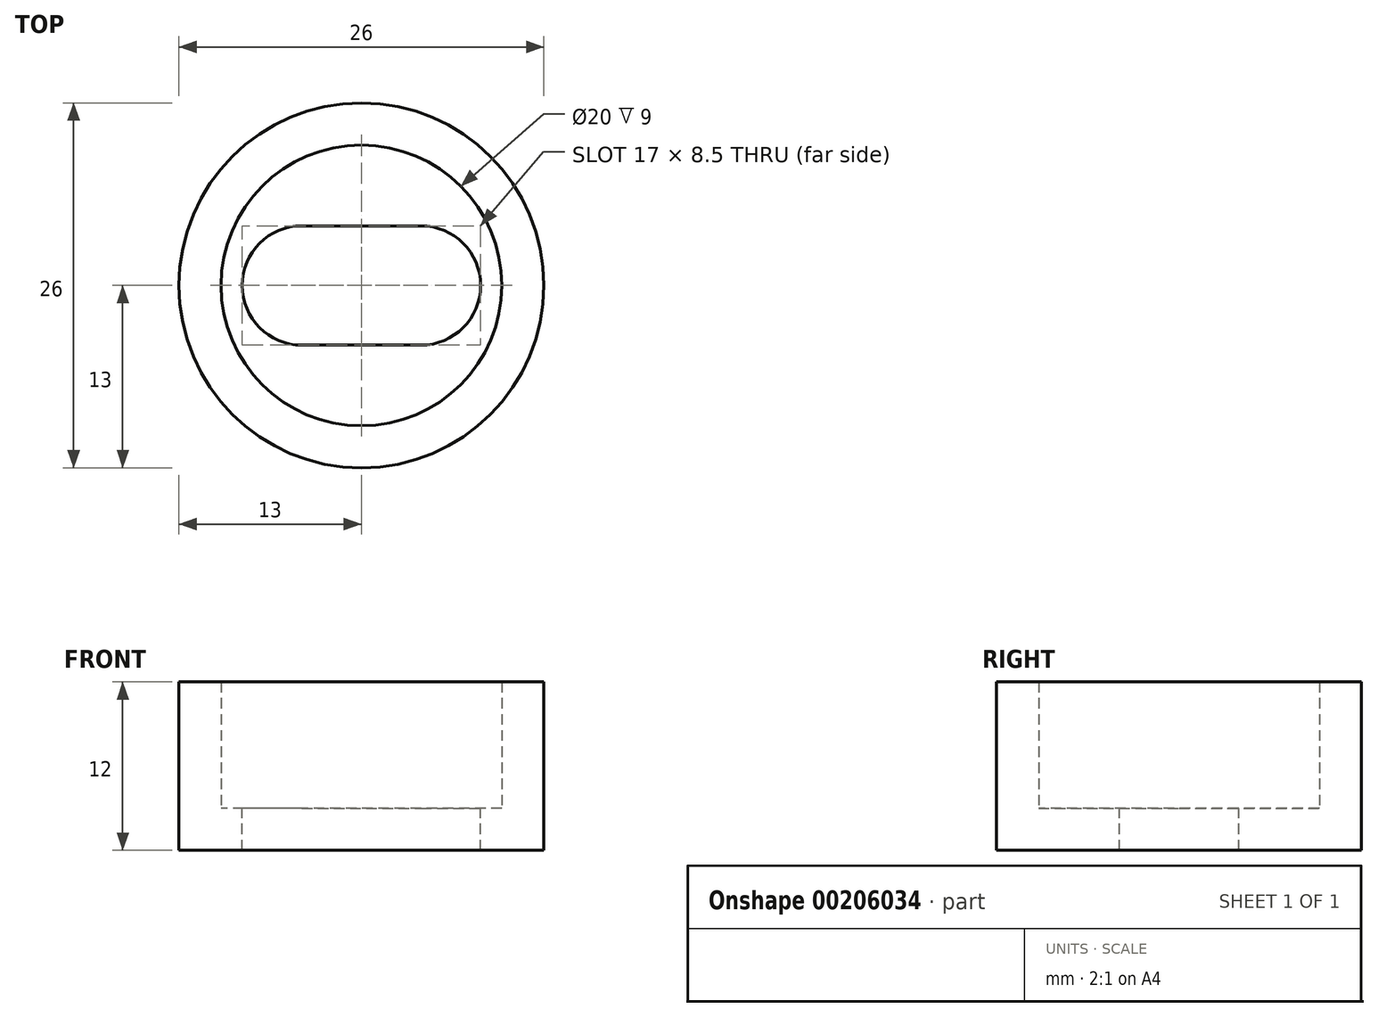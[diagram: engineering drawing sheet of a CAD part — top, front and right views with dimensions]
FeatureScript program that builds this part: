
annotation { "Feature Type Name" : "Feature", "Feature Type Description" : "" }
export const myFeature = defineFeature(function(context is Context, id is Id, definition is map)
    precondition{}
    {
        {
            var Q0;
            Q0=qCreatedBy(makeId("Top.planeOp"),FACE);
            var sketch = newSketch(context, id + "F0", { "sketchPlane" : qUnion([Q0])});
            skCircle(sketch, "E0", {"center": v(0, 0) * mm, "radius": 13 * mm});
            skSolve(sketch);
        }
        {
            var Q0;
            Q0=makeQuery(id+"F0.imprint","IMPRINT",FACE,{"disambiguationData":[TD([[makeQuery(id+"F0.imprint","IMPRINT",EDGE,{"derivedFrom":sQuery(id+"F0.wireOp",EDGE,"E0")}),1.0]])]});
            extrude(context, id + "F1", {"entities" : qUnion([Q0]), "depth" : 3 * mm});
        }
        {
            var Q0;
            Q0=makeQuery(id+"F1.opExtrude","CAP_FACE",FACE,{"disambiguationData":[OSD([sQuery(id+"F0.wireOp",EDGE,"E0")])],"isStart":false});
            var sketch = newSketch(context, id + "F2", { "sketchPlane" : qUnion([Q0])});
            skLineSegment(sketch, "E1", {"start": v(-4.25, 4.25) * mm, "end": v(4.25, 4.25) * mm});
            skLineSegment(sketch, "E2", {"start": v(-4.25, -4.25) * mm, "end": v(4.25, -4.25) * mm});
            skArc(sketch, "E3", {"start": v(-4.25, 4.25) * mm, "mid": v(-8.5, 0) * mm, "end": v(-4.25, -4.25) * mm});
            skArc(sketch, "E4", {"start": v(4.25, -4.25) * mm, "mid": v(8.5, 0) * mm, "end": v(4.25, 4.25) * mm});
            skSolve(sketch);
        }
        {
            var Q0;
            Q0=makeQuery(id+"F2.imprint","IMPRINT",FACE,{"disambiguationData":[TD([[makeQuery(id+"F2.imprint","IMPRINT",EDGE,{"derivedFrom":sQuery(id+"F2.wireOp",EDGE,"E1")}),-1.0]])]});
            extrude(context, id + "F3", {"entities" : qUnion([Q0]), "operationType" : NewBodyOperationType.REMOVE, "oppositeDirection" : true, "depth" : 3 * mm});
        }
        {
            var Q0;
            Q0=makeQuery(id+"F1.opExtrude","CAP_FACE",FACE,{"disambiguationData":[OSD([sQuery(id+"F0.wireOp",EDGE,"E0")])],"isStart":false});
            var sketch = newSketch(context, id + "F4", { "sketchPlane" : qUnion([Q0])});
            skCircle(sketch, "E5", {"center": v(0, 0) * mm, "radius": 13 * mm});
            skCircle(sketch, "E6", {"center": v(0, 0) * mm, "radius": 10 * mm});
            skSolve(sketch);
        }
        {
            var Q0;
            Q0=makeQuery(id+"F4.imprint","IMPRINT",FACE,{"disambiguationData":[TD([[makeQuery(id+"F4.imprint","IMPRINT",EDGE,{"derivedFrom":sQuery(id+"F4.wireOp",EDGE,"E5")}),1.0]])]});
            extrude(context, id + "F5", {"entities" : qUnion([Q0]), "operationType" : NewBodyOperationType.ADD, "depth" : 9 * mm});
        }
    });
